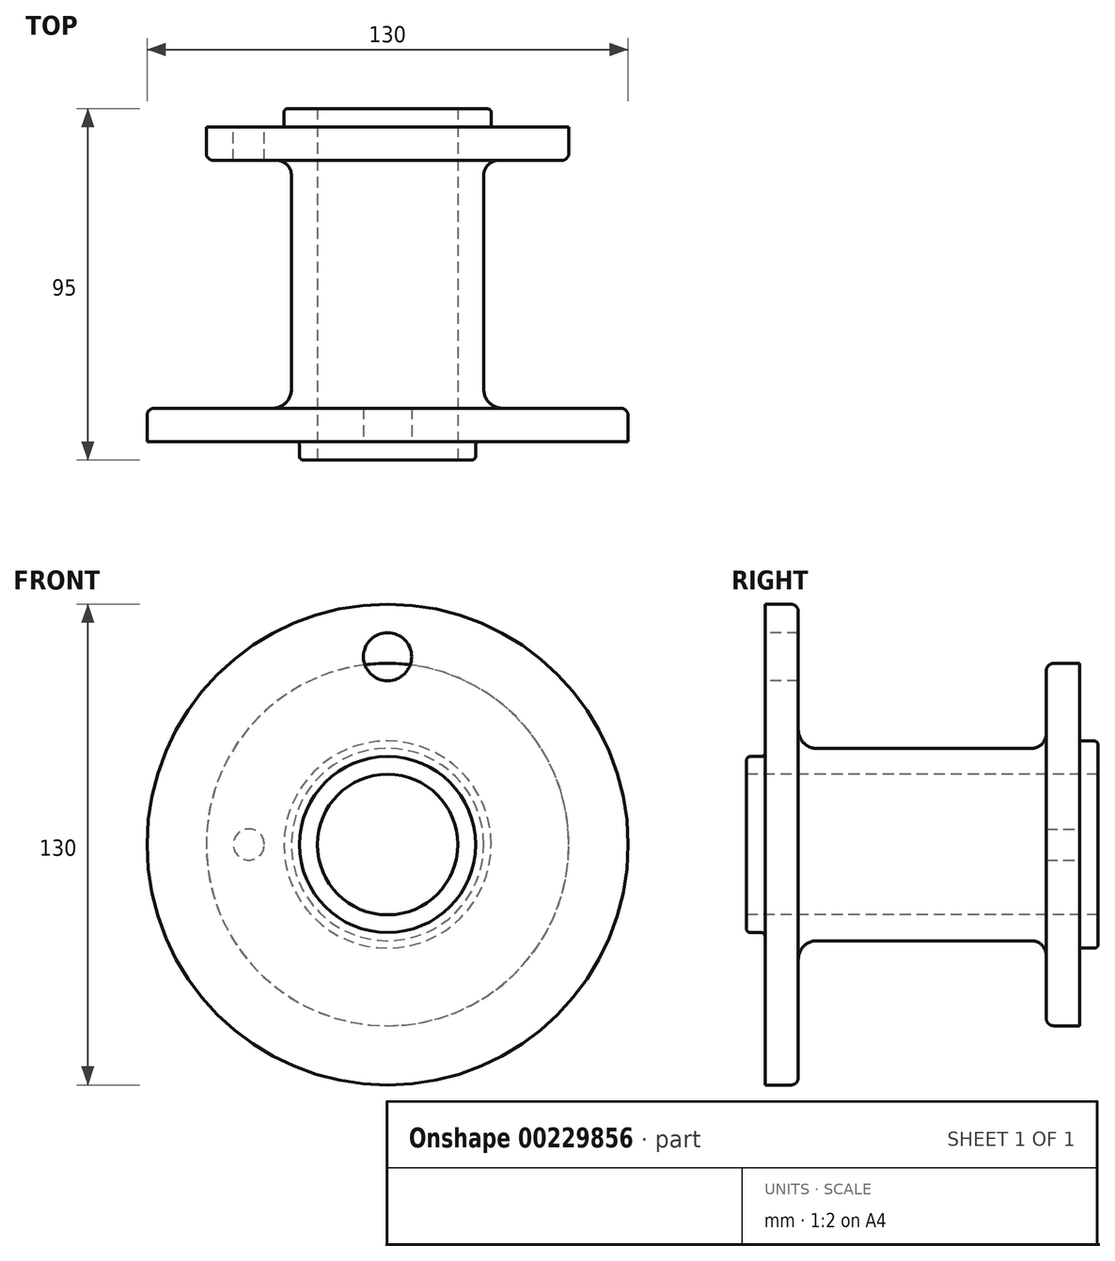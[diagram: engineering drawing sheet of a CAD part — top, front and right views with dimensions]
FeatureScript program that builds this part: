
annotation { "Feature Type Name" : "Feature", "Feature Type Description" : "" }
export const myFeature = defineFeature(function(context is Context, id is Id, definition is map)
    precondition{}
    {
        {
            var Q0;
            Q0=qCreatedBy(makeId("Right.planeOp"),FACE);
            var sketch = newSketch(context, id + "F0", { "sketchPlane" : qUnion([Q0])});
            skLineSegment(sketch, "E0", {"start": v(85, 26) * mm, "end": v(85, 49) * mm});
            skLineSegment(sketch, "E1", {"start": v(7, 65) * mm, "end": v(0, 65) * mm});
            skLineSegment(sketch, "E2", {"start": v(0, 65) * mm, "end": v(0, 24.8) * mm});
            skPoint(sketch, "E3.orphan", {"position": v(0, 0) * mm});
            skPoint(sketch, "E4.orphan", {"position": v(85, 0) * mm});
            skLineSegment(sketch, "E5", {"start": v(-61.85, 0) * mm, "end": v(66.72, 0) * mm, "construction": true});
            skLineSegment(sketch, "E6", {"start": v(85, 19) * mm, "end": v(0, 19) * mm});
            skLineSegment(sketch, "E7", {"start": v(14, 26) * mm, "end": v(72, 26) * mm});
            skLineSegment(sketch, "E8", {"start": v(9, 63) * mm, "end": v(9, 31) * mm});
            skLineSegment(sketch, "E9", {"start": v(85, 49) * mm, "end": v(78, 49) * mm});
            skLineSegment(sketch, "E10", {"start": v(76, 47) * mm, "end": v(76, 30) * mm});
            skPoint(sketch, "E11.visualSharp", {"position": v(9, 26) * mm});
            skArc(sketch, "E11.filletArc", {"start": v(9, 31) * mm, "mid": v(10.46, 27.46) * mm, "end": v(14, 26) * mm});
            skPoint(sketch, "E12.visualSharp", {"position": v(9, 65) * mm});
            skArc(sketch, "E12.filletArc", {"start": v(9, 63) * mm, "mid": v(8.41, 64.41) * mm, "end": v(7, 65) * mm});
            skLineSegment(sketch, "E13", {"start": v(89, 28) * mm, "end": v(90.9, 28) * mm});
            skLineSegment(sketch, "E14", {"start": v(90, 27) * mm, "end": v(90, 19) * mm});
            skLineSegment(sketch, "E15", {"start": v(90, 19) * mm, "end": v(85, 19) * mm});
            skPoint(sketch, "E16.visualSharp", {"position": v(85, 28) * mm});
            skPoint(sketch, "E17.visualSharp", {"position": v(90, 28) * mm});
            skArc(sketch, "E17.filletArc", {"start": v(90, 27) * mm, "mid": v(89.7, 27.7) * mm, "end": v(89, 28) * mm});
            skLineSegment(sketch, "E18", {"start": v(-1, 23.8) * mm, "end": v(-4, 23.8) * mm});
            skLineSegment(sketch, "E19", {"start": v(-5, 22.8) * mm, "end": v(-5, 19) * mm});
            skLineSegment(sketch, "E20", {"start": v(-5, 19) * mm, "end": v(0, 19) * mm});
            skPoint(sketch, "E21.visualSharp", {"position": v(-5, 23.8) * mm});
            skArc(sketch, "E21.filletArc", {"start": v(-4, 23.8) * mm, "mid": v(-4.7, 23.5) * mm, "end": v(-5, 22.8) * mm});
            skPoint(sketch, "E22.visualSharp", {"position": v(0, 23.8) * mm});
            skArc(sketch, "E22.filletArc", {"start": v(-1, 23.8) * mm, "mid": v(-0.3, 24.1) * mm, "end": v(0, 24.8) * mm});
            skLineSegment(sketch, "E23", {"start": v(85, 28) * mm, "end": v(85, 26) * mm});
            skLineSegment(sketch, "E24", {"start": v(90.9, 28) * mm, "end": v(85, 28) * mm});
            skPoint(sketch, "E25.visualSharp", {"position": v(76, 26) * mm});
            skArc(sketch, "E25.filletArc", {"start": v(72, 26) * mm, "mid": v(74.83, 27.17) * mm, "end": v(76, 30) * mm});
            skLineSegment(sketch, "E26", {"start": v(105.18, 37.5) * mm, "end": v(65.86, 37.5) * mm, "construction": true});
            skLineSegment(sketch, "E27", {"start": v(-5.13, 50.8) * mm, "end": v(13.32, 50.8) * mm, "construction": true});
            skPoint(sketch, "E28.visualSharp", {"position": v(76, 49) * mm});
            skArc(sketch, "E28.filletArc", {"start": v(78, 49) * mm, "mid": v(76.59, 48.41) * mm, "end": v(76, 47) * mm});
            skSolve(sketch);
        }
        {
            var Q0;
            Q0=qSketchRegion(id+"F0",true);
            var Q1;
            Q1=sQuery(id+"F0.wireOp",EDGE,"E5");
            revolve(context, id + "F1", {"entities" : qUnion([Q0]), "axis" : qUnion([Q1]), "revolveType" : RevolveType.FULL});
        }
        {
            var Q0;
            Q0=makeQuery(id+"F1.opRevolve","SWEPT_FACE",FACE,{"disambiguationData":[OSD([sQuery(id+"F0.wireOp",EDGE,"E0")])]});
            var sketch = newSketch(context, id + "F2", { "sketchPlane" : qUnion([Q0])});
            skPoint(sketch, "E29", {"position": v(37.5, 0) * mm});
            skSolve(sketch);
        }
        {
            var Q0;
            Q0=sQuery(id+"F2.wireOp",VERTEX,"E29");
            var Q1;
            Q1=makeQuery(id+"F1.opRevolve","SWEPT_BODY",BODY,{"disambiguationData":[OSD([sQuery(id+"F0.wireOp",EDGE,"E0"),sQuery(id+"F0.wireOp",EDGE,"HLiBYaoR-hPD8-fsvN-p6GD-5fYDkM4Fedih"),sQuery(id+"F0.wireOp",EDGE,"FoxjxBjz-NUPa-fNWZ-N56x-yW2nvaL2xadz"),sQuery(id+"F0.wireOp",EDGE,"E1"),sQuery(id+"F0.wireOp",EDGE,"E2"),sQuery(id+"F0.wireOp",EDGE,"94b84a5b-fda0-446a-8ec9-4f86c6f93436.filletArc"),sQuery(id+"F0.wireOp",EDGE,"hWWw9Ktu-YnIE-uSGB-SsMi-DuxsHIGMdIkd")])]});
            hole(context, id + "F3", {"style" : HoleStyle.SIMPLE, "endStyle" : HoleEndStyle.BLIND, "standardTappedOrClearance" : lookupTablePath({ "standard" : "ISO", "fit" : "Close", "size" : "M8", "type" : "Clearance" }), "standardBlindInLast" : lookupTablePath({ "fit" : "Close", "standard" : "ISO", "size" : "M8", "type" : "Clearance" }), "holeDiameter" : 8.4 * mm, "holeDepth" : 15 * mm, "locations" : qUnion([Q0]), "scope" : qUnion([Q1])});
        }
        {
            var Q0;
            Q0=qCreatedBy(makeId("Front.planeOp"),FACE);
            var sketch = newSketch(context, id + "F4", { "sketchPlane" : qUnion([Q0])});
            skCircle(sketch, "E30", {"center": v(0, 50.8) * mm, "radius": 6.5 * mm});
            skSolve(sketch);
        }
        {
            var Q0;
            Q0=qSketchRegion(id+"F4",true);
            extrude(context, id + "F5", {"entities" : qUnion([Q0]), "operationType" : NewBodyOperationType.REMOVE, "oppositeDirection" : true, "depth" : 18 * mm});
        }
    });
